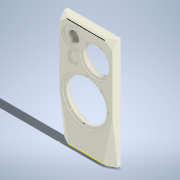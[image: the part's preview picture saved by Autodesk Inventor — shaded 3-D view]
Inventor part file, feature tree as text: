
AUTODESK INVENTOR PART (.ipt)
format: ipt  version: 2022 (Build 260153000, 153)  size: 558,080 bytes
history: native  units: mm
features: other x24, sketch x15, chamfer x4, fillet x4, extrude x3, hole x3
ambient origin geometry x8: Origin, YZ Plane, XZ Plane, XY Plane, X Axis, Y Axis, Z Axis, Center Point
bodies: Body1 (feature_tree)
feature tree (53):
  other  "Аннотации"
  extrude  "Выдавливание2"  Depth=186.0mm
  hole  "Отверстие1"  [1 undecoded]
  extrude  "Выдавливание3"  Depth=102.0mm
  hole  "Отверстие3"  [1 undecoded]
  hole  "Отверстие4"  [1 undecoded]
  extrude  "Выдавливание4"  Depth=5.0mm
  sketch  "Эскиз9"
  sketch  "Эскиз10"
  other  "РабТочка1"
  other  "РабТочка2"
  other  "РабТочка3"
  other  "РабПлоскость1"
  other  "Разделение1"
  sketch  "Эскиз11"
  other  "РабТочка4"
  other  "РабТочка5"
  sketch  "Эскиз12"
  other  "РабТочка6"
  other  "РабПлоскость2"
  other  "Разделение2"
  sketch  "Эскиз13"
  sketch  "Эскиз14"
  sketch  "Эскиз15"
  other  "РабПлоскость3"
  other  "Разделение3"
  sketch  "Эскиз16"
  other  "РабПлоскость4"
  other  "Разделение4"
  chamfer  "Фаска1"  Distance=5.0mm
  chamfer  "Фаска2"  Distance=5.0mm
  chamfer  "Фаска3"  Distance=250.0mm
  chamfer  "Фаска4"  Distance=520.0mm
  fillet  "Сопряжение1"  Radius=120.0mm
  fillet  "Сопряжение2"  Radius=50.0mm
  fillet  "Сопряжение3"  Radius=40.0mm
  fillet  "Сопряжение4"  Radius=60.0mm
  sketch  "Эскиз17"
  sketch  "Эскиз1"
  sketch  "Эскиз3"
  sketch  "Эскиз4"
  sketch  "Эскиз6"
  sketch  "Эскиз7"
  sketch  "Эскиз8"
  other  "Линейный размер 1"
  other  "Линейный размер 2"
  other  "Линейный размер 3"
  other  "Линейный размер 4"
  other  "Линейный размер 5"
  other  "Линейный размер 6"
  other  "Линейный размер 7"
  other  "Линейный размер 8"
  other  "Линейный размер 9"
note: 3 required parameter values undecoded (feature->parameter linkage not recoverable at this tier; creation-order binding heuristic only, values carry confidence <= 0.55)
